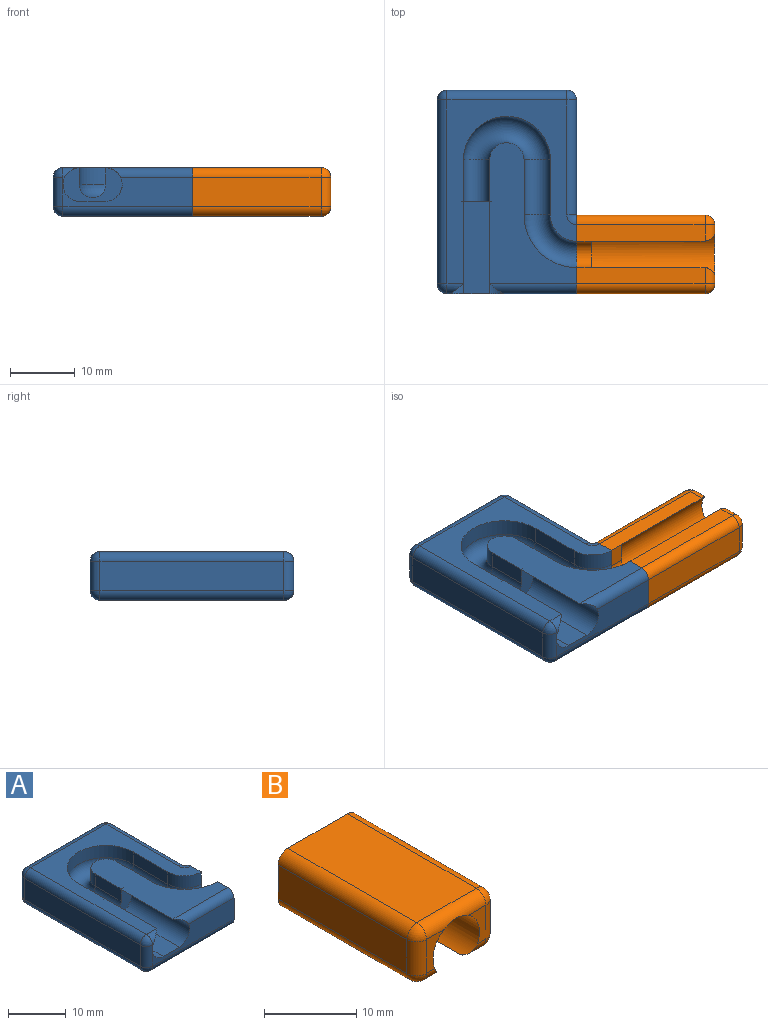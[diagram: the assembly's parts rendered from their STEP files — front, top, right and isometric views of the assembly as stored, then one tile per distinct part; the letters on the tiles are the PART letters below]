
ASSEMBLY  parts=2 mates=1
PART A: 48 faces, bbox 21.5x31.4x7.5 mm
  f0: plane 20.02x4.49mm, normal (0,-1,0), area 59mm2, adj f3,f4,f5,f15,f28,f31,f47
  f1: plane 0.06x0mm, normal (0,1,0), area 0mm2, adj f2,f3,f14
  f2: plane 21.78x13.48mm, normal (0,0,1), area 147.5mm2, adj f1,f3,f14,f15,f18,f22,f26,f47
  f3: cylinder r=2.6mm len=14.29mm, axis (0,1,0), area 115.2mm2, adj f0,f1,f2,f4,f11,f47
  f4: plane 14.29x3.94mm, normal (0,0,1), area 56.2mm2, adj f0,f3,f5,f11
  f5: cylinder r=2.6mm len=14.29mm, axis (0,1,0), area 115.2mm2, adj f0,f4,f6,f9,f10,f11,f30
  f6: plane 28.38x20.02mm, normal (0,0,1), area 182.5mm2, adj f5,f10,f13,f15,f16,f20,f24,f30
  f7: plane 28.38x4.49mm, normal (-1,0,0), area 127.5mm2, adj f31,f32,f36,f37
  f8: plane 28.38x20.02mm, normal (0,0,-1), area 539.3mm2, adj f15,f28,f32,f35,f38,f39
  f9: plane 1.1x0.25mm, normal (0,-1,0), area 0.1mm2, adj f5,f30,f31
  f10: plane 0.06x0mm, normal (0,1,0), area 0mm2, adj f5,f6,f13
  f11: plane 9.14x5.21mm, normal (0,-1,0), area 24.7mm2, adj f3,f4,f5,f12,f13,f14
  f12: cylinder r=2.03mm len=6.35mm, axis (0,-1,0), area 40.5mm2, adj f11,f13,f14,f17
  f13: plane 6.35x2.6mm, normal (1,0,0), area 16.5mm2, adj f6,f10,f11,f12,f16
  f14: plane 6.35x2.6mm, normal (-1,0,0), area 16.5mm2, adj f1,f2,f11,f12,f18
  f15: plane 12.12x7.49mm, normal (1,0,0), area 71.8mm2, adj f0,f2,f6,f8,f23,f24,f25,f26
  f16: cylinder r=6.71mm len=13.41mm, axis (0,0,-1), area 54.9mm2, adj f6,f13,f17,f20
  f17: torus R=4.67mm, axis (0,0,-1), area 93.7mm2, adj f12,f16,f18,f21
  f18: cylinder r=2.64mm len=5.28mm, axis (0,0,-1), area 21.6mm2, adj f2,f14,f17,f22
  f19: plane 17.74x4.49mm, normal (1,0,0), area 79.7mm2, adj f23,f39,f43,f45
  f20: plane 8.5x2.6mm, normal (-1,0,0), area 22.1mm2, adj f6,f16,f21,f24
  f21: cylinder r=2.03mm len=8.5mm, axis (0,-1,0), area 54.2mm2, adj f17,f20,f22,f25
  f22: plane 8.5x2.6mm, normal (1,0,0), area 22.1mm2, adj f2,f18,f21,f26
  f23: cylinder r=0.03mm len=4.49mm, axis (0,0,1), area 0.2mm2, adj f15,f19,f35,f46
  f24: cylinder r=4.07mm len=4.07mm, axis (0,0,1), area 16.6mm2, adj f6,f15,f20,f25
  f25: torus R=6.1mm, axis (0,0,1), area 61.1mm2, adj f15,f21,f24,f26
  f26: cylinder r=8.13mm len=8.13mm, axis (0,0,1), area 33.2mm2, adj f2,f15,f22,f25
  f27: plane 18.49x4.49mm, normal (0,1,0), area 83.1mm2, adj f37,f38,f42,f43
  f28: cylinder r=1.5mm len=20.02mm, axis (-1,0,0), area 47.2mm2, adj f0,f8,f15,f29
  f29: sphere r=1.5mm, area 3.5mm2, adj f28,f31,f32
  f30: cylinder r=1.5mm len=2.6mm, axis (1,0,0), area 2.9mm2, adj f5,f6,f9,f33
  f31: cylinder r=1.5mm len=4.49mm, axis (0,0,1), area 10.6mm2, adj f0,f7,f9,f29,f33
  f32: cylinder r=1.5mm len=28.38mm, axis (0,1,0), area 66.9mm2, adj f7,f8,f29,f34
  f33: sphere r=1.5mm, area 3.5mm2, adj f30,f31,f36
  f34: sphere r=1.5mm, area 3.5mm2, adj f32,f37,f38
  f35: torus R=1.53mm, axis (0,0,1), area 2.1mm2, adj f8,f15,f23,f39
  f36: cylinder r=1.5mm len=28.38mm, axis (0,-1,0), area 66.9mm2, adj f6,f7,f33,f40
  f37: cylinder r=1.5mm len=4.49mm, axis (0,0,1), area 10.6mm2, adj f7,f27,f34,f40
  f38: cylinder r=1.5mm len=18.49mm, axis (1,0,0), area 43.6mm2, adj f8,f27,f34,f41
  f39: cylinder r=1.5mm len=17.74mm, axis (0,1,0), area 41.8mm2, adj f8,f19,f35,f41
  f40: sphere r=1.5mm, area 3.5mm2, adj f36,f37,f42
  f41: sphere r=1.5mm, area 3.5mm2, adj f38,f39,f43
  f42: cylinder r=1.5mm len=18.49mm, axis (-1,0,0), area 43.6mm2, adj f6,f27,f40,f44
  f43: cylinder r=1.5mm len=4.49mm, axis (0,0,-1), area 10.6mm2, adj f19,f27,f41,f44
  f44: sphere r=1.5mm, area 3.5mm2, adj f42,f43,f45
  f45: cylinder r=1.5mm len=17.74mm, axis (0,-1,0), area 41.8mm2, adj f6,f19,f44,f46
  f46: torus R=1.53mm, axis (0,0,1), area 2.1mm2, adj f6,f15,f23,f45
  f47: cylinder r=1.5mm len=13.48mm, axis (1,0,0), area 28.6mm2, adj f0,f2,f3,f15
PART B: 26 faces, bbox 12.1x21.3x7.5 mm
  f0: plane 4.5x2.75mm, normal (0,-1,0), area 6.2mm2, adj f5,f13,f18,f23
  f1: plane 19.8x4.5mm, normal (1,0,0), area 89.1mm2, adj f12,f16,f22,f25
  f2: plane 19.8x9.14mm, normal (0,0,1), area 181mm2, adj f12,f19,f23,f25
  f3: plane 19.8x4.5mm, normal (-1,0,0), area 89.1mm2, adj f12,f14,f18,f19
  f4: plane 19.8x2.54mm, normal (0,0,-1), area 50.3mm2, adj f5,f9,f12,f13,f14
  f5: cylinder r=3.57mm len=19.05mm, axis (0,1,0), area 343.2mm2, adj f0,f4,f6,f7,f8,f13,f17,f23
  f6: plane 19.8x2.54mm, normal (0,0,-1), area 50.3mm2, adj f5,f10,f12,f16,f17
  f7: plane 4.5x2.75mm, normal (0,-1,0), area 6.2mm2, adj f5,f17,f22,f23
  f8: plane 7.14x6.5mm, normal (0,-1,0), area 19.8mm2, adj f5,f9,f10,f11
  f9: plane 2.93x2.25mm, normal (1,0,0), area 6.6mm2, adj f4,f8,f11,f12
  f10: plane 2.93x2.25mm, normal (-1,0,0), area 6.6mm2, adj f6,f8,f11,f12
  f11: cylinder r=2.03mm len=4.06mm, axis (0,-1,0), area 14.4mm2, adj f8,f9,f10,f12
  f12: plane 12.14x7.5mm, normal (0,1,0), area 70.7mm2, adj f1,f2,f3,f4,f6,f9,f10,f11
  f13: cylinder r=1.5mm len=2.54mm, axis (-1,0,0), area 4.7mm2, adj f0,f4,f5,f15
  f14: cylinder r=1.5mm len=19.8mm, axis (0,-1,0), area 46.7mm2, adj f3,f4,f12,f15
  f15: sphere r=1.5mm, area 3.5mm2, adj f13,f14,f18
  f16: cylinder r=1.5mm len=19.8mm, axis (0,-1,0), area 46.7mm2, adj f1,f6,f12,f20
  f17: cylinder r=1.5mm len=2.54mm, axis (-1,0,0), area 4.7mm2, adj f5,f6,f7,f20
  f18: cylinder r=1.5mm len=4.5mm, axis (0,0,1), area 10.6mm2, adj f0,f3,f15,f21
  f19: cylinder r=1.5mm len=19.8mm, axis (0,1,0), area 46.7mm2, adj f2,f3,f12,f21
  f20: sphere r=1.5mm, area 3.5mm2, adj f16,f17,f22
  f21: sphere r=1.5mm, area 3.5mm2, adj f18,f19,f23
  f22: cylinder r=1.5mm len=4.5mm, axis (0,0,-1), area 10.6mm2, adj f1,f7,f20,f24
  f23: cylinder r=1.5mm len=9.14mm, axis (1,0,0), area 20.3mm2, adj f0,f2,f5,f7,f21,f24
  f24: sphere r=1.5mm, area 3.5mm2, adj f22,f23,f25
  f25: cylinder r=1.5mm len=19.8mm, axis (0,1,0), area 46.7mm2, adj f1,f2,f12,f24
PLACE A t=(9.61,0.04,0.02)mm
PLACE B rot(axis=(0.71,-0.71,0),180deg) t=(27.33,-8.19,-2.11)mm
MATE slider A.f15 <-> B.f12  axis (1,0,0) through (25.08,-8.19,5.7)mm
